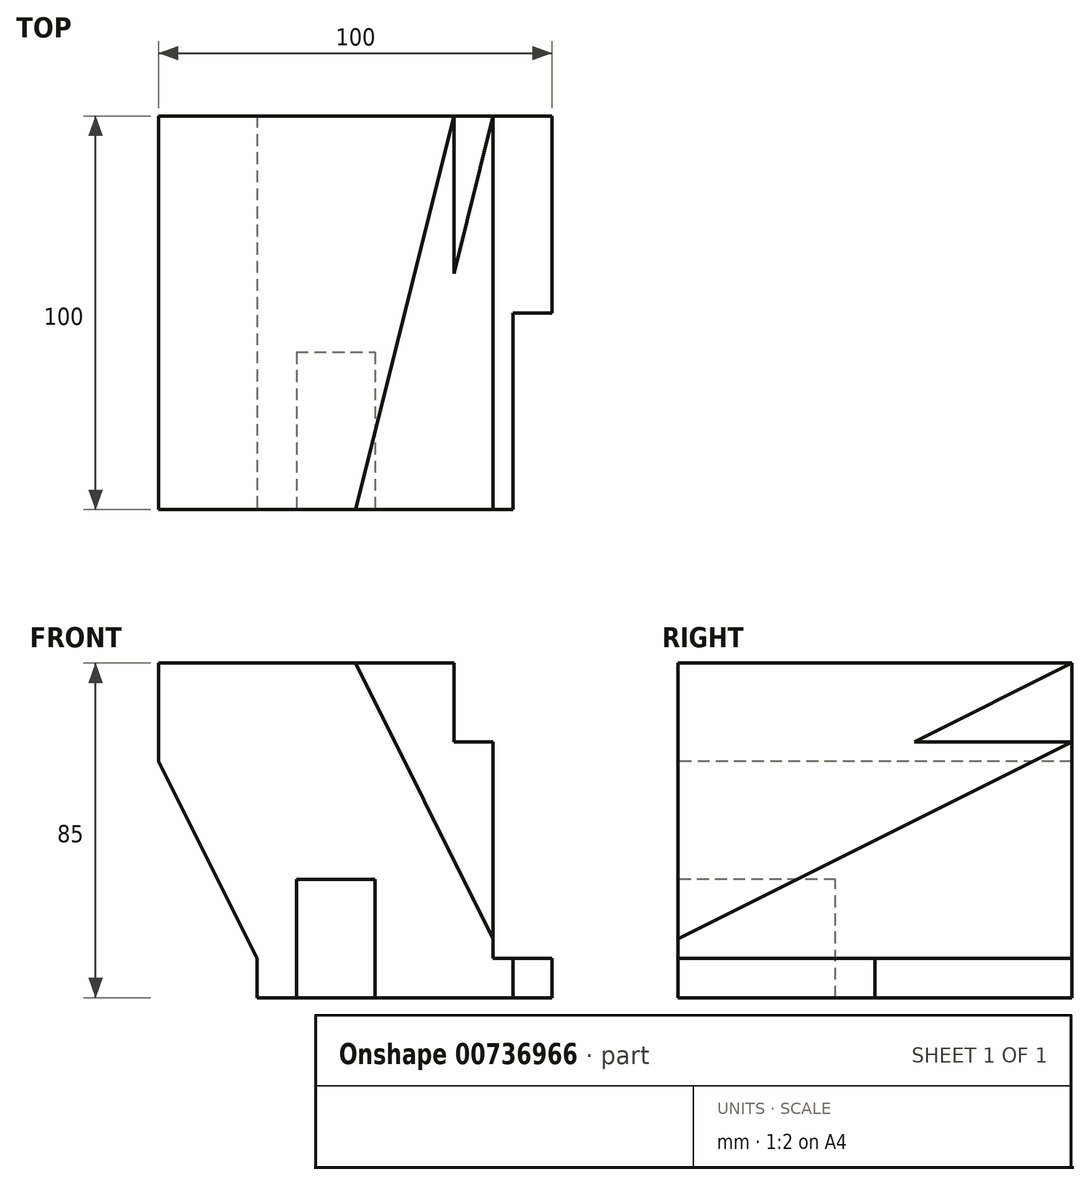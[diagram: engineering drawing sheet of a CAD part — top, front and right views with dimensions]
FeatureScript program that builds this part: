
annotation { "Feature Type Name" : "Feature", "Feature Type Description" : "" }
export const myFeature = defineFeature(function(context is Context, id is Id, definition is map)
    precondition{}
    {
        {
            var Q0;
            Q0=qCreatedBy(makeId("Right.planeOp"),FACE);
            var sketch = newSketch(context, id + "F0", { "sketchPlane" : qUnion([Q0])});
            skLineSegment(sketch, "E0.bottom", {"start": v(0, 0) * mm, "end": v(100, 0) * mm});
            skLineSegment(sketch, "E0.top", {"start": v(0, 85) * mm, "end": v(100, 85) * mm});
            skLineSegment(sketch, "E0.left", {"start": v(0, 0) * mm, "end": v(0, 85) * mm});
            skLineSegment(sketch, "E0.right", {"start": v(100, 0) * mm, "end": v(100, 85) * mm});
            skSolve(sketch);
        }
        {
            var Q0;
            Q0=makeQuery(id+"F0.imprint","IMPRINT",FACE,{"disambiguationData":[TD([[makeQuery(id+"F0.imprint","IMPRINT",EDGE,{"derivedFrom":sQuery(id+"F0.wireOp",EDGE,"E0.bottom")}),1.0]])]});
            extrude(context, id + "F1", {"entities" : qUnion([Q0]), "depth" : 75 * mm, "offsetDistance" : 25 * mm, "hasSecondDirection" : true, "secondDirectionOppositeDirection" : true, "secondDirectionDepth" : 25 * mm});
        }
        {
            var Q0;
            Q0=qCreatedBy(makeId("Front.planeOp"),FACE);
            var sketch = newSketch(context, id + "F2", { "sketchPlane" : qUnion([Q0])});
            skLineSegment(sketch, "E1", {"start": v(-25, 60) * mm, "end": v(0, 10) * mm});
            skLineSegment(sketch, "E2", {"start": v(0, 10) * mm, "end": v(0, 0) * mm});
            skLineSegment(sketch, "E3", {"start": v(0, 0) * mm, "end": v(-25, 0) * mm});
            skLineSegment(sketch, "E4", {"start": v(-25, 0) * mm, "end": v(-25, 60) * mm});
            skSolve(sketch);
        }
        {
            var Q0;
            Q0 = qSketchRegion(id + "F2", true);
            extrude(context, id + "F3", {"entities" : qUnion([Q0]), "operationType" : NewBodyOperationType.REMOVE, "endBound" : BoundingType.UP_TO_NEXT, "oppositeDirection" : true, "depth" : 25 * mm, "offsetDistance" : 25 * mm});
        }
        {
            var Q0;
            Q0=qCreatedBy(makeId("Front.planeOp"),FACE);
            var sketch = newSketch(context, id + "F4", { "sketchPlane" : qUnion([Q0])});
            skLineSegment(sketch, "E5.bottom", {"start": v(10, 0) * mm, "end": v(30, 0) * mm});
            skLineSegment(sketch, "E5.top", {"start": v(10, 30) * mm, "end": v(30, 30) * mm});
            skLineSegment(sketch, "E5.left", {"start": v(10, 0) * mm, "end": v(10, 30) * mm});
            skLineSegment(sketch, "E5.right", {"start": v(30, 0) * mm, "end": v(30, 30) * mm});
            skSolve(sketch);
        }
        {
            var Q0;
            Q0 = qSketchRegion(id + "F4", true);
            extrude(context, id + "F5", {"entities" : qUnion([Q0]), "operationType" : NewBodyOperationType.REMOVE, "oppositeDirection" : true, "depth" : 40 * mm, "offsetDistance" : 25 * mm});
        }
        {
            var Q0;
            Q0=qCreatedBy(makeId("Front.planeOp"),FACE);
            var sketch = newSketch(context, id + "F6", { "sketchPlane" : qUnion([Q0])});
            skLineSegment(sketch, "E6", {"start": v(60, 10) * mm, "end": v(75, 10) * mm});
            skLineSegment(sketch, "E7.0", {"start": v(75, 85) * mm, "end": v(50, 85) * mm});
            skLineSegment(sketch, "E8.0", {"start": v(75, 10) * mm, "end": v(75, 85) * mm});
            skPoint(sketch, "E9.orphan", {"position": v(-25, 85) * mm});
            skPoint(sketch, "E10.orphan", {"position": v(75, 0) * mm});
            skLineSegment(sketch, "E11", {"start": v(50, 85) * mm, "end": v(50, 65) * mm});
            skLineSegment(sketch, "E12", {"start": v(50, 65) * mm, "end": v(60, 65) * mm});
            skLineSegment(sketch, "E13", {"start": v(60, 65) * mm, "end": v(60, 10) * mm});
            skSolve(sketch);
        }
        {
            var Q0;
            Q0 = qSketchRegion(id + "F6", true);
            extrude(context, id + "F7", {"entities" : qUnion([Q0]), "operationType" : NewBodyOperationType.REMOVE, "endBound" : BoundingType.UP_TO_NEXT, "oppositeDirection" : true, "depth" : 25 * mm, "offsetDistance" : 25 * mm});
        }
        {
            var Q0;
            Q0=qCreatedBy(makeId("Top.planeOp"),FACE);
            var sketch = newSketch(context, id + "F8", { "sketchPlane" : qUnion([Q0])});
            skLineSegment(sketch, "E14", {"start": v(65, 0) * mm, "end": v(65, 50) * mm});
            skLineSegment(sketch, "E15", {"start": v(65, 50) * mm, "end": v(75, 50) * mm});
            skLineSegment(sketch, "E16", {"start": v(75, 50) * mm, "end": v(75, 0) * mm});
            skLineSegment(sketch, "E17", {"start": v(75, 0) * mm, "end": v(65, 0) * mm});
            skSolve(sketch);
        }
        {
            var Q0;
            Q0 = qSketchRegion(id + "F8", true);
            extrude(context, id + "F9", {"entities" : qUnion([Q0]), "operationType" : NewBodyOperationType.REMOVE, "depth" : 25 * mm, "offsetDistance" : 25 * mm});
        }
        {
            var Q0;
            Q0=makeQuery(id+"F1.opExtrude","SWEPT_FACE",FACE,{"disambiguationData":[OSD([sQuery(id+"F0.wireOp",EDGE,"E0.top")])]});
            var sketch = newSketch(context, id + "F10", { "sketchPlane" : qUnion([Q0])});
            skLineSegment(sketch, "E18.bottom", {"start": v(15, 80) * mm, "end": v(50, 80) * mm});
            skLineSegment(sketch, "E18.top", {"start": v(15, 70) * mm, "end": v(50, 70) * mm});
            skLineSegment(sketch, "E18.left", {"start": v(15, 80) * mm, "end": v(15, 70) * mm, "construction": true});
            skLineSegment(sketch, "E18.right", {"start": v(50, 80) * mm, "end": v(50, 70) * mm, "construction": true});
            skLineSegment(sketch, "E19", {"start": v(5.1, 75) * mm, "end": v(73.45, 75) * mm, "construction": true});
            skArc(sketch, "E20", {"start": v(50, 70) * mm, "mid": v(55, 75) * mm, "end": v(50, 80) * mm});
            skArc(sketch, "E21", {"start": v(15, 80) * mm, "mid": v(10, 75) * mm, "end": v(15, 70) * mm});
            skSolve(sketch);
        }
        {
            var Q0;
            Q0=qCreatedBy(makeId("Front.planeOp"),FACE);
            var sketch = newSketch(context, id + "F11", { "sketchPlane" : qUnion([Q0])});
            skLineSegment(sketch, "E22", {"start": v(60, 0) * mm, "end": v(60, 65) * mm});
            skLineSegment(sketch, "E23", {"start": v(60, 65) * mm, "end": v(0, 65) * mm});
            skLineSegment(sketch, "E24", {"start": v(0, 65) * mm, "end": v(0, 0) * mm});
            skLineSegment(sketch, "E25", {"start": v(0, 0) * mm, "end": v(60, 0) * mm});
            skSolve(sketch);
        }
        {
            var Q0;
            {var subQ2=sQuery(id+"F10.wireOp",EDGE,"E18.bottom");Q0=makeQuery(id+"F10.imprint","IMPRINT",FACE,{"disambiguationData":[TD([[makeQuery(id+"F10.imprint","IMPRINT",EDGE,{"derivedFrom":subQ2}),1.0]])]});}
            var sketch = newSketch(context, id + "F12", { "sketchPlane" : qUnion([Q0])});
            skLineSegment(sketch, "E26.bottom", {"start": v(12.21, 40) * mm, "end": v(30.4, 40) * mm});
            skLineSegment(sketch, "E26.top", {"start": v(12.21, 20) * mm, "end": v(30.4, 20) * mm});
            skLineSegment(sketch, "E26.left", {"start": v(12.21, 40) * mm, "end": v(12.21, 20) * mm});
            skLineSegment(sketch, "E26.right", {"start": v(30.4, 40) * mm, "end": v(30.4, 20) * mm});
            skSolve(sketch);
        }
        {
            var Q0;
            Q0=qCreatedBy(makeId("Front.planeOp"),FACE);
            var sketch = newSketch(context, id + "F13", { "sketchPlane" : qUnion([Q0])});
            skLineSegment(sketch, "E27", {"start": v(25, 85) * mm, "end": v(60, 10) * mm});
            skSolve(sketch);
        }
        {
            var Q0;
            Q0=makeQuery(id+"F7.boolean.opBoolean","COPY",VERTEX,{"derivedFrom":makeQuery(id+"F7.opExtrude","CAP_VERTEX",VERTEX,{"disambiguationData":[OSD([sQuery(id+"F0.wireOp",EDGE,"E0.right"),sQuery(id+"F6.wireOp",EDGE,"E7.0"),sQuery(id+"F6.wireOp",EDGE,"E11")])],"isStart":false})});
            var Q1;
            Q1=makeQuery(id+"F7.boolean.opBoolean","COPY",VERTEX,{"derivedFrom":makeQuery(id+"F7.opExtrude","CAP_VERTEX",VERTEX,{"disambiguationData":[OSD([sQuery(id+"F0.wireOp",EDGE,"E0.right"),sQuery(id+"F6.wireOp",EDGE,"E12"),sQuery(id+"F6.wireOp",EDGE,"E13")])],"isStart":false})});
            var Q2;
            Q2=sQuery(id+"F13.wireOp",VERTEX,"E27.start");
            cPlane(context, id + "F14", {"entities" : qUnion([Q0, Q1, Q2]), "cplaneType" : CPlaneType.THREE_POINT, "offset" : 25 * mm, "width" : 150 * mm, "height" : 150 * mm});
        }
        {
            var Q0;
            Q0=qCreatedBy(id+"F14.planeOp",FACE);
            var sketch = newSketch(context, id + "F15", { "sketchPlane" : qUnion([Q0])});
            skLineSegment(sketch, "E28", {"start": v(84.9, 57.02) * mm, "end": v(35.33, 62.43) * mm});
            skLineSegment(sketch, "E29", {"start": v(35.33, 62.43) * mm, "end": v(13.17, 64.85) * mm});
            skLineSegment(sketch, "E30", {"start": v(115.64, 53.67) * mm, "end": v(95.15, 55.9) * mm});
            skLineSegment(sketch, "E31", {"start": v(115.64, 53.67) * mm, "end": v(74.66, 35.78) * mm});
            skLineSegment(sketch, "E32", {"start": v(13.17, 64.85) * mm, "end": v(13.17, -13.42) * mm});
            skLineSegment(sketch, "E33", {"start": v(115.64, 31.3) * mm, "end": v(13.17, -13.42) * mm});
            skLineSegment(sketch, "E34", {"start": v(74.66, 35.78) * mm, "end": v(115.64, 31.3) * mm});
            skLineSegment(sketch, "E35", {"start": v(84.9, 57.02) * mm, "end": v(95.15, 55.9) * mm});
            skPoint(sketch, "E36.end.orphan", {"position": v(13.17, -24.6) * mm});
            skPoint(sketch, "E36.start.orphan", {"position": v(13.17, -19) * mm});
            skPoint(sketch, "E37.orphan", {"position": v(33.67, 62.6) * mm});
            skSolve(sketch);
        }
        {
            var Q0;
            Q0 = qSketchRegion(id + "F15", true);
            extrude(context, id + "F16", {"entities" : qUnion([Q0]), "operationType" : NewBodyOperationType.REMOVE, "depth" : 25 * mm, "offsetDistance" : 25 * mm});
        }
    });
